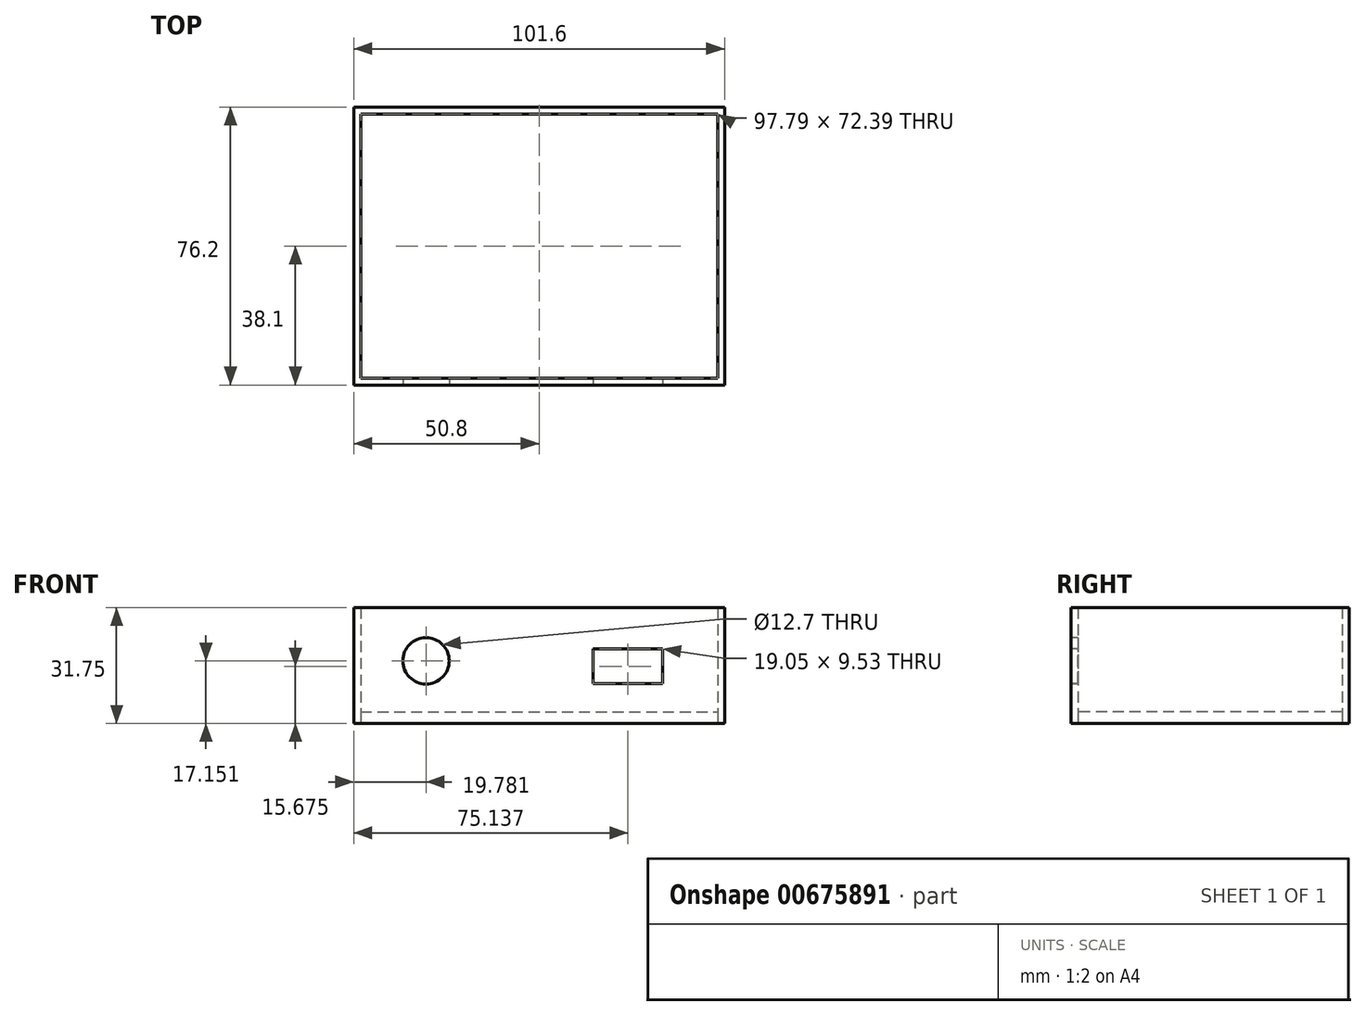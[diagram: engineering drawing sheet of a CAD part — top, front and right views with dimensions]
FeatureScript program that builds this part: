
annotation { "Feature Type Name" : "Feature", "Feature Type Description" : "" }
export const myFeature = defineFeature(function(context is Context, id is Id, definition is map)
    precondition{}
    {
        {
            var Q0;
            Q0=qCreatedBy(makeId("Top.planeOp"),FACE);
            var sketch = newSketch(context, id + "F0", { "sketchPlane" : qUnion([Q0])});
            skLineSegment(sketch, "E0.bottom", {"start": v(-50.8, 38.1) * mm, "end": v(50.8, 38.1) * mm});
            skLineSegment(sketch, "E0.top", {"start": v(-50.8, -38.1) * mm, "end": v(50.8, -38.1) * mm});
            skLineSegment(sketch, "E0.left", {"start": v(-50.8, 38.1) * mm, "end": v(-50.8, -38.1) * mm});
            skLineSegment(sketch, "E0.right", {"start": v(50.8, 38.1) * mm, "end": v(50.8, -38.1) * mm});
            skPoint(sketch, "E0.middle", {"position": v(0, 0) * mm});
            skLineSegment(sketch, "E1.bottom", {"start": v(-48.9, 36.2) * mm, "end": v(48.9, 36.2) * mm});
            skLineSegment(sketch, "E1.top", {"start": v(-48.9, -36.2) * mm, "end": v(48.9, -36.2) * mm});
            skLineSegment(sketch, "E1.left", {"start": v(-48.9, 36.2) * mm, "end": v(-48.9, -36.2) * mm});
            skLineSegment(sketch, "E1.right", {"start": v(48.9, 36.2) * mm, "end": v(48.9, -36.2) * mm});
            skSolve(sketch);
        }
        {
            var Q0;
            Q0=makeQuery(id+"F0.imprint","IMPRINT",FACE,{"disambiguationData":[TD([[makeQuery(id+"F0.imprint","IMPRINT",EDGE,{"derivedFrom":sQuery(id+"F0.wireOp",EDGE,"E0.bottom")}),-1.0]])]});
            extrude(context, id + "F1", {"entities" : qUnion([Q0]), "depth" : 31.75 * mm, "offsetDistance" : 25.4 * mm});
        }
        {
            var Q0;
            Q0=makeQuery(id+"F1.opExtrude","SWEPT_FACE",FACE,{"disambiguationData":[OSD([sQuery(id+"F0.wireOp",EDGE,"E0.top")])]});
            var sketch = newSketch(context, id + "F2", { "sketchPlane" : qUnion([Q0])});
            skLineSegment(sketch, "E2.bottom", {"start": v(33.86, 10.91) * mm, "end": v(14.81, 10.91) * mm});
            skLineSegment(sketch, "E2.top", {"start": v(33.86, 20.44) * mm, "end": v(14.81, 20.44) * mm});
            skLineSegment(sketch, "E2.left", {"start": v(33.86, 10.91) * mm, "end": v(33.86, 20.44) * mm});
            skLineSegment(sketch, "E2.right", {"start": v(14.81, 10.91) * mm, "end": v(14.81, 20.44) * mm});
            skPoint(sketch, "E2.middle", {"position": v(24.34, 15.68) * mm});
            skCircle(sketch, "E3", {"center": v(-31.02, 17.15) * mm, "radius": 3.97 * mm});
            skSolve(sketch);
        }
        {
            var Q0;
            Q0=sQuery(id+"F2.wireOp",VERTEX,"E3.center");
            var Q1;
            Q1=makeQuery(id+"F1.opExtrude","SWEPT_BODY",BODY,{"disambiguationData":[OSD([sQuery(id+"F0.wireOp",EDGE,"E0.bottom"),sQuery(id+"F0.wireOp",EDGE,"E0.top"),sQuery(id+"F0.wireOp",EDGE,"E0.left"),sQuery(id+"F0.wireOp",EDGE,"E0.right"),sQuery(id+"F0.wireOp",EDGE,"E1.bottom"),sQuery(id+"F0.wireOp",EDGE,"E1.top"),sQuery(id+"F0.wireOp",EDGE,"E1.left"),sQuery(id+"F0.wireOp",EDGE,"E1.right")])]});
            hole(context, id + "F3", {"style" : HoleStyle.SIMPLE, "endStyle" : HoleEndStyle.BLIND, "holeDiameter" : 12.7 * mm, "majorDiameter" : 6.35 * mm, "holeDepth" : 12.7 * mm, "isTappedThrough" : true, "tappedDepth" : 12.7 * mm, "tapClearance" : 3, "locations" : qUnion([Q0]), "scope" : qUnion([Q1])});
        }
        {
            var Q0;
            Q0=makeQuery(id+"F0.imprint","IMPRINT",FACE,{"disambiguationData":[TD([[makeQuery(id+"F0.imprint","IMPRINT",EDGE,{"derivedFrom":sQuery(id+"F0.wireOp",EDGE,"E1.bottom")}),-1.0]])]});
            extrude(context, id + "F4", {"entities" : qUnion([Q0]), "depth" : 3.17 * mm, "offsetDistance" : 25.4 * mm});
        }
        {
            var Q0;
            Q0=makeQuery(id+"F2.imprint","IMPRINT",FACE,{"disambiguationData":[TD([[makeQuery(id+"F2.imprint","IMPRINT",EDGE,{"derivedFrom":sQuery(id+"F2.wireOp",EDGE,"E2.bottom")}),-1.0]])]});
            extrude(context, id + "F5", {"entities" : qUnion([Q0]), "operationType" : NewBodyOperationType.REMOVE, "endBound" : BoundingType.UP_TO_NEXT, "oppositeDirection" : true, "depth" : 51.3 * mm, "offsetDistance" : 25.4 * mm});
        }
    });
